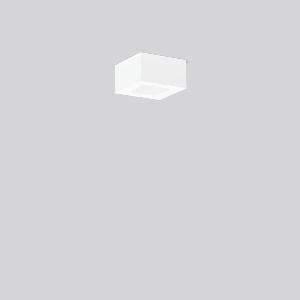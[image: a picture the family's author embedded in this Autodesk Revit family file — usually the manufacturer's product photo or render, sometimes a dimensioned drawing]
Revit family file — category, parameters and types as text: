
# Revit family: toledo_flat_square_a_901551_002_b573
name_source: partatom
category: Lighting Fixtures
units: mm (PartAtom-declared; Revit-internal decimal feet)

## family parameters
Cut with Voids When Loaded = No
Host = Face
Light Source = No
Part Type = Normal
Room Calculation Point = No
Round Connector Dimension = Use Diameter
Shared = No

## types (1)
- TOLEDO FLAT square A (1 x LED Modul 830, 420 lm, 3000)
    Apparent Load = 5 VA
    CIE Flux Codes = 49 80 96 100 100
    Color Rendering = 80
    Color Temperature = 3000
    Default Elevation = 1800 mm
    Description = Series: TOLEDO FLAT square
Ultra thin surface mounted downlight. Surface mounted housing: sheet steel, powder-coated. Square cover plate: die-cast aluminium, powder coated. Light guide and diffuser made of non-yellowing PMMA, opal matt. Suitable for Ceiling mounting, Wall (surface). Driver integrated. 
Colour: white
Length: 110 mm
Width: 110 mm
Height: 58 mm
Lamp: LED
Socket: without socket
Colour temperature: 3000K
Colour rendering index (CRI): 80
System power: 5 W
Rated luminous flux: 420 lm
Luminous efficiency: 84 lm/W
Control gear: Regulated power supply
Protection class: II
Type of protection: IP 40
    Height = 58 mm
    Lamp = 1 x LED Modul 830
    Lamp Light Flux = 420 lm
    Lamp count = 1
    Length = 110 mm
    Lifetime = 50000 h
    Luminous efficacy = 84 lm/W
    Manufacturer = RZB
    ModVariant = No
    Model = 901551.002
    Mounting Place = Ceiling
    Mounting Type = Surface mounted
    Number of Poles = 1
    OnlyDefault = Yes
    Power Factor = 1
    Product Name = TOLEDO FLAT square A
    Product group = Surface mounted downlights
    ProductGroupID = 302
    Protection Class = Protection class II
    Protection Degree = IP 40
    RLX_Detail_Level = 1
    RLX_Emergency_Light_Flux = 0 lm
    RLX_Emergency_Type = 0
    RLX_Emergency_Type_DB = No
    RlxData = <blob elided: 12801 chars, md5=f596976a>
    Socket = socket
    Standby Power = 0 W
    System Light Flux = 420 lm
    System Power = 5 W
    Type Comments = Product without accessories
    Type Image = 901551.002.jpg
    URL = http://relux.com
    VarID = ---
    Voltage = 230 V
    Voltage Range = 220-240 V
    Weight = 0.00 kg
    Width = 110 mm

## geometry (parser evidence)
native form markers: Sweep x9
no freeform markers — native parametric forms only
